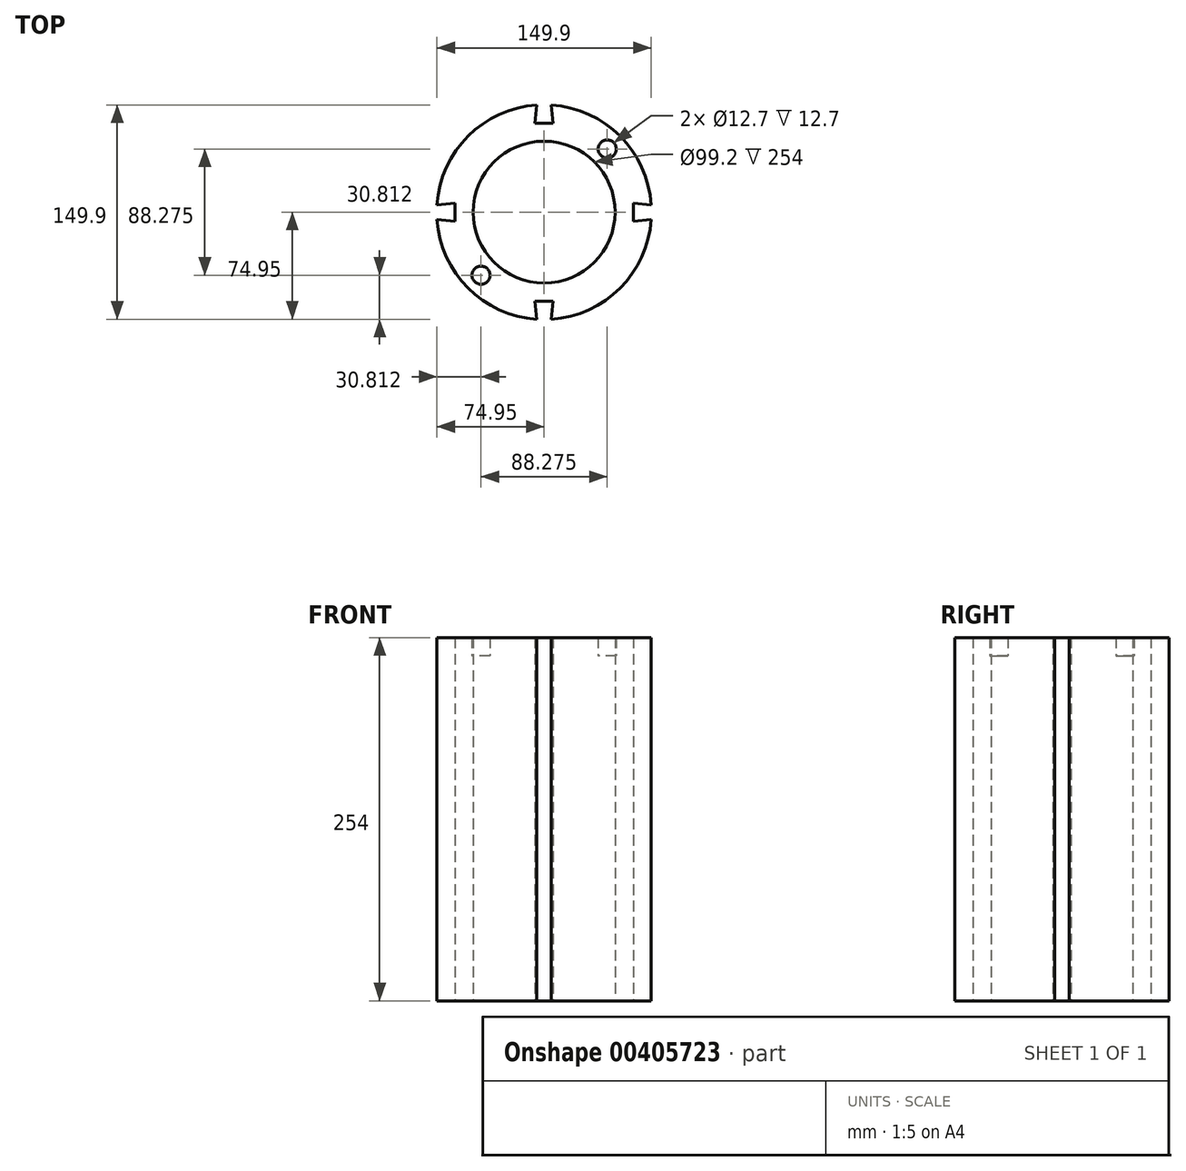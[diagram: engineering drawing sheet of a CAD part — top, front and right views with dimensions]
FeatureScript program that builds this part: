
annotation { "Feature Type Name" : "Feature", "Feature Type Description" : "" }
export const myFeature = defineFeature(function(context is Context, id is Id, definition is map)
    precondition{}
    {
        {
            var Q0;
            Q0=qCreatedBy(makeId("Top.planeOp"),FACE);
            var sketch = newSketch(context, id + "F0", { "sketchPlane" : qUnion([Q0])});
            skArc(sketch, "E0", {"start": v(-74.95, -5.08) * mm, "mid": v(-53.12, -53.12) * mm, "end": v(-5.08, -74.95) * mm});
            skCircle(sketch, "E1", {"center": v(0, 0) * mm, "radius": 49.6 * mm});
            skLineSegment(sketch, "E2", {"start": v(-62.3, 0) * mm, "end": v(-62.3, -6.35) * mm});
            skLineSegment(sketch, "E3", {"start": v(-62.3, -6.35) * mm, "end": v(-62.3, 6.35) * mm});
            skLineSegment(sketch, "E4", {"start": v(-62.3, 6.35) * mm, "end": v(-74.95, 5.08) * mm});
            skLineSegment(sketch, "E5.MirrorCS", {"start": v(-62.3, -6.35) * mm, "end": v(-74.95, -5.08) * mm});
            skLineSegment(sketch, "E6.MirrorCS", {"start": v(62.3, -6.35) * mm, "end": v(62.3, 6.35) * mm});
            skLineSegment(sketch, "E7.MirrorCS", {"start": v(62.3, -6.35) * mm, "end": v(74.95, -5.08) * mm});
            skLineSegment(sketch, "E8.MirrorCS", {"start": v(62.3, 6.35) * mm, "end": v(74.95, 5.08) * mm});
            skArc(sketch, "E9.trimOffspring", {"start": v(74.95, 5.08) * mm, "mid": v(53.12, 53.12) * mm, "end": v(5.08, 74.95) * mm});
            skLineSegment(sketch, "E10.MirrorCS", {"start": v(-6.35, -62.3) * mm, "end": v(-5.08, -74.95) * mm});
            skLineSegment(sketch, "E11.MirrorCS", {"start": v(-6.35, -62.3) * mm, "end": v(6.35, -62.3) * mm});
            skLineSegment(sketch, "E12.MirrorCS", {"start": v(6.35, -62.3) * mm, "end": v(5.08, -74.95) * mm});
            skLineSegment(sketch, "E13.MirrorCS", {"start": v(-6.35, 62.3) * mm, "end": v(6.35, 62.3) * mm});
            skLineSegment(sketch, "E14.MirrorCS", {"start": v(6.35, 62.3) * mm, "end": v(5.08, 74.95) * mm});
            skLineSegment(sketch, "E15.MirrorCS", {"start": v(-6.35, 62.3) * mm, "end": v(-5.08, 74.95) * mm});
            skArc(sketch, "E16.trimOffspring", {"start": v(-5.08, 74.95) * mm, "mid": v(-53.12, 53.12) * mm, "end": v(-74.95, 5.08) * mm});
            skArc(sketch, "E17.trimOffspring", {"start": v(5.08, -74.95) * mm, "mid": v(53.12, -53.12) * mm, "end": v(74.95, -5.08) * mm});
            skSolve(sketch);
        }
        {
            var Q0;
            Q0=makeQuery(id+"F0.imprint","IMPRINT",FACE,{"disambiguationData":[TD([[makeQuery(id+"F0.imprint","IMPRINT",EDGE,{"derivedFrom":sQuery(id+"F0.wireOp",EDGE,"E0")}),1.0]])]});
            extrude(context, id + "F1", {"entities" : qUnion([Q0]), "depth" : 241.3 * mm});
        }
        {
            var Q0;
            Q0=makeQuery(id+"F1.opExtrude","CAP_FACE",FACE,{"disambiguationData":[OSD([sQuery(id+"F0.wireOp",EDGE,"E0"),sQuery(id+"F0.wireOp",EDGE,"E1"),sQuery(id+"F0.wireOp",EDGE,"E3"),sQuery(id+"F0.wireOp",EDGE,"E4"),sQuery(id+"F0.wireOp",EDGE,"E5.MirrorCS"),sQuery(id+"F0.wireOp",EDGE,"E6.MirrorCS"),sQuery(id+"F0.wireOp",EDGE,"E7.MirrorCS"),sQuery(id+"F0.wireOp",EDGE,"E8.MirrorCS"),sQuery(id+"F0.wireOp",EDGE,"E9.trimOffspring"),sQuery(id+"F0.wireOp",EDGE,"E11.MirrorCS"),sQuery(id+"F0.wireOp",EDGE,"E10.MirrorCS"),sQuery(id+"F0.wireOp",EDGE,"E12.MirrorCS"),sQuery(id+"F0.wireOp",EDGE,"E13.MirrorCS"),sQuery(id+"F0.wireOp",EDGE,"E14.MirrorCS"),sQuery(id+"F0.wireOp",EDGE,"E15.MirrorCS"),sQuery(id+"F0.wireOp",EDGE,"E16.trimOffspring"),sQuery(id+"F0.wireOp",EDGE,"E17.trimOffspring")])],"isStart":false});
            var sketch = newSketch(context, id + "F2", { "sketchPlane" : qUnion([Q0])});
            skCircle(sketch, "E18", {"center": v(-44.14, 44.14) * mm, "radius": 6.35 * mm});
            skCircle(sketch, "E19.MirrorC", {"center": v(44.14, 44.14) * mm, "radius": 6.35 * mm});
            skCircle(sketch, "E20.MirrorC", {"center": v(-44.14, -44.14) * mm, "radius": 6.35 * mm});
            skCircle(sketch, "E21.MirrorC", {"center": v(44.14, -44.14) * mm, "radius": 6.35 * mm});
            skSolve(sketch);
        }
        {
            var Q0;
            Q0=makeQuery(id+"F2.imprint","IMPRINT",FACE,{"disambiguationData":[TD([[makeQuery(id+"F2.imprint","IMPRINT",EDGE,{"derivedFrom":sQuery(id+"F2.wireOp",EDGE,"E18")}),1.0]])]});
            var Q1;
            Q1=makeQuery(id+"F2.imprint","IMPRINT",FACE,{"disambiguationData":[TD([[makeQuery(id+"F2.imprint","IMPRINT",EDGE,{"derivedFrom":sQuery(id+"F2.wireOp",EDGE,"E20.MirrorC")}),-1.0]])]});
            var Q2;
            Q2=makeQuery(id+"F2.imprint","IMPRINT",FACE,{"disambiguationData":[TD([[makeQuery(id+"F2.imprint","IMPRINT",EDGE,{"derivedFrom":sQuery(id+"F2.wireOp",EDGE,"E21.MirrorC")}),1.0]])]});
            var Q3;
            Q3=makeQuery(id+"F2.imprint","IMPRINT",FACE,{"disambiguationData":[TD([[makeQuery(id+"F2.imprint","IMPRINT",EDGE,{"derivedFrom":sQuery(id+"F2.wireOp",EDGE,"E19.MirrorC")}),-1.0]])]});
            extrude(context, id + "F3", {"entities" : qUnion([Q0, Q1, Q2, Q3]), "operationType" : NewBodyOperationType.ADD, "depth" : 12.7 * mm});
        }
    });
